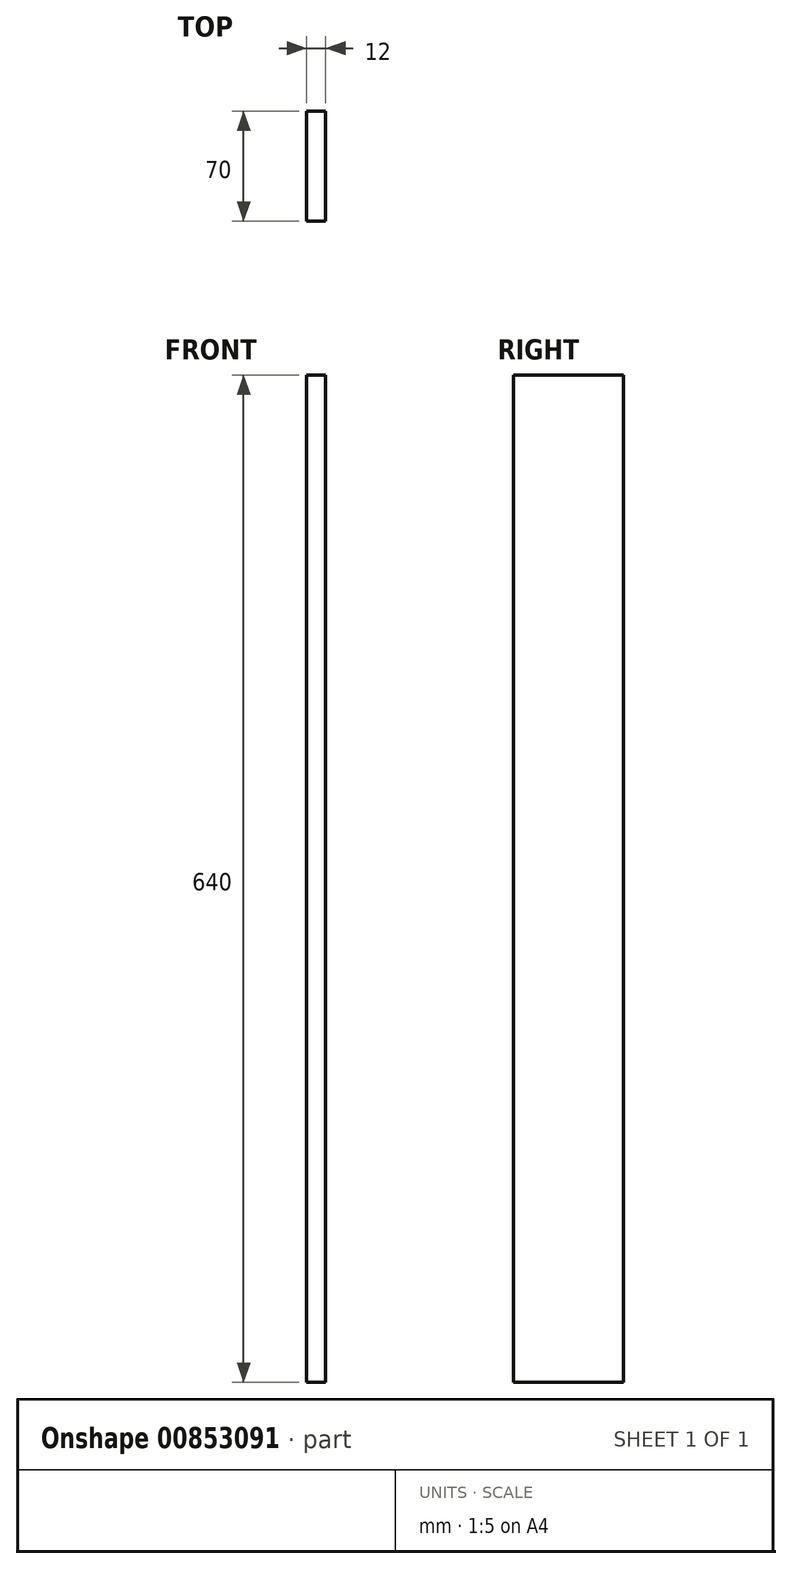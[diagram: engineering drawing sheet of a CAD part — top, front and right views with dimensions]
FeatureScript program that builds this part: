
annotation { "Feature Type Name" : "Feature", "Feature Type Description" : "" }
export const myFeature = defineFeature(function(context is Context, id is Id, definition is map)
    precondition{}
    {
        {
            var Q0;
            Q0=qCreatedBy(makeId("Right.planeOp"),FACE);
            var sketch = newSketch(context, id + "F0", { "sketchPlane" : qUnion([Q0])});
            skLineSegment(sketch, "E0.bottom", {"start": v(35, -320) * mm, "end": v(-35, -320) * mm});
            skLineSegment(sketch, "E0.top", {"start": v(35, 320) * mm, "end": v(-35, 320) * mm});
            skLineSegment(sketch, "E0.left", {"start": v(35, -320) * mm, "end": v(35, 320) * mm});
            skLineSegment(sketch, "E0.right", {"start": v(-35, -320) * mm, "end": v(-35, 320) * mm});
            skPoint(sketch, "E0.middle", {"position": v(0, 0) * mm});
            skSolve(sketch);
        }
        {
            var Q0;
            Q0=makeQuery(id+"F0.imprint","IMPRINT",FACE,{"disambiguationData":[TD([[makeQuery(id+"F0.imprint","IMPRINT",EDGE,{"derivedFrom":sQuery(id+"F0.wireOp",EDGE,"E0.bottom")}),-1.0]])]});
            extrude(context, id + "F1", {"entities" : qUnion([Q0]), "depth" : 6 * mm, "offsetDistance" : 25 * mm, "hasSecondDirection" : true, "secondDirectionOppositeDirection" : true, "secondDirectionDepth" : 6 * mm});
        }
    });
